# Revit family: 210_Gourmet-MW white
name_source: partatom
category: Mechanical Equipment
revit_build: Autodesk Revit 2018 (Build: 20170223_1515(x64)
units: mm (PartAtom-declared; Revit-internal decimal feet)

## family parameters
Always vertical = Yes
Cut with Voids When Loaded = No
Part Type = Breaks Into
Room Calculation Point = No
Round Connector Dimension = Use Diameter
Shared = No
Work Plane-Based = No

## types (1)
- 125-13630
    CAT0 = Yes
    D = 125 mm
    Description = Ventilator Gourmet-MW white
    H = 129 mm  [stored 0.423228 ft]
    H2 = 20 mm  [stored 0.0656168 ft]
    H3 = 23 mm  [stored 0.0754593 ft]
    L = 600 mm  [stored 1.9685 ft]
    L1 = 300 mm  [stored 0.984252 ft]
    L2 = 580 mm  [stored 1.90289 ft]
    MC Product Code = 125-13630
    Manufacturer = Flexit
    QmdConnectorList = 201;D
    W = 500 mm
    W10 = 92 mm  [stored 0.301837 ft]
    W3 = 85 mm  [stored 0.278871 ft]
    W4 = 170 mm  [stored 0.557743 ft]
    W6 = 200 mm  [stored 0.656168 ft]
    W7 = 277 mm  [stored 0.908793 ft]
    W9 = 10 mm  [stored 0.0328084 ft]
    magiPartTypeId = 210
    magiProductFamilyId = Gourmet-MW white
    magiProductId = Gourmet-MW White 125

note: [stored X ft] marks values corroborated as IEEE doubles in the binary element streams (Revit-internal decimal feet)

## geometry (parser evidence)
native form markers: Sweep x2
no freeform markers — native parametric forms only
